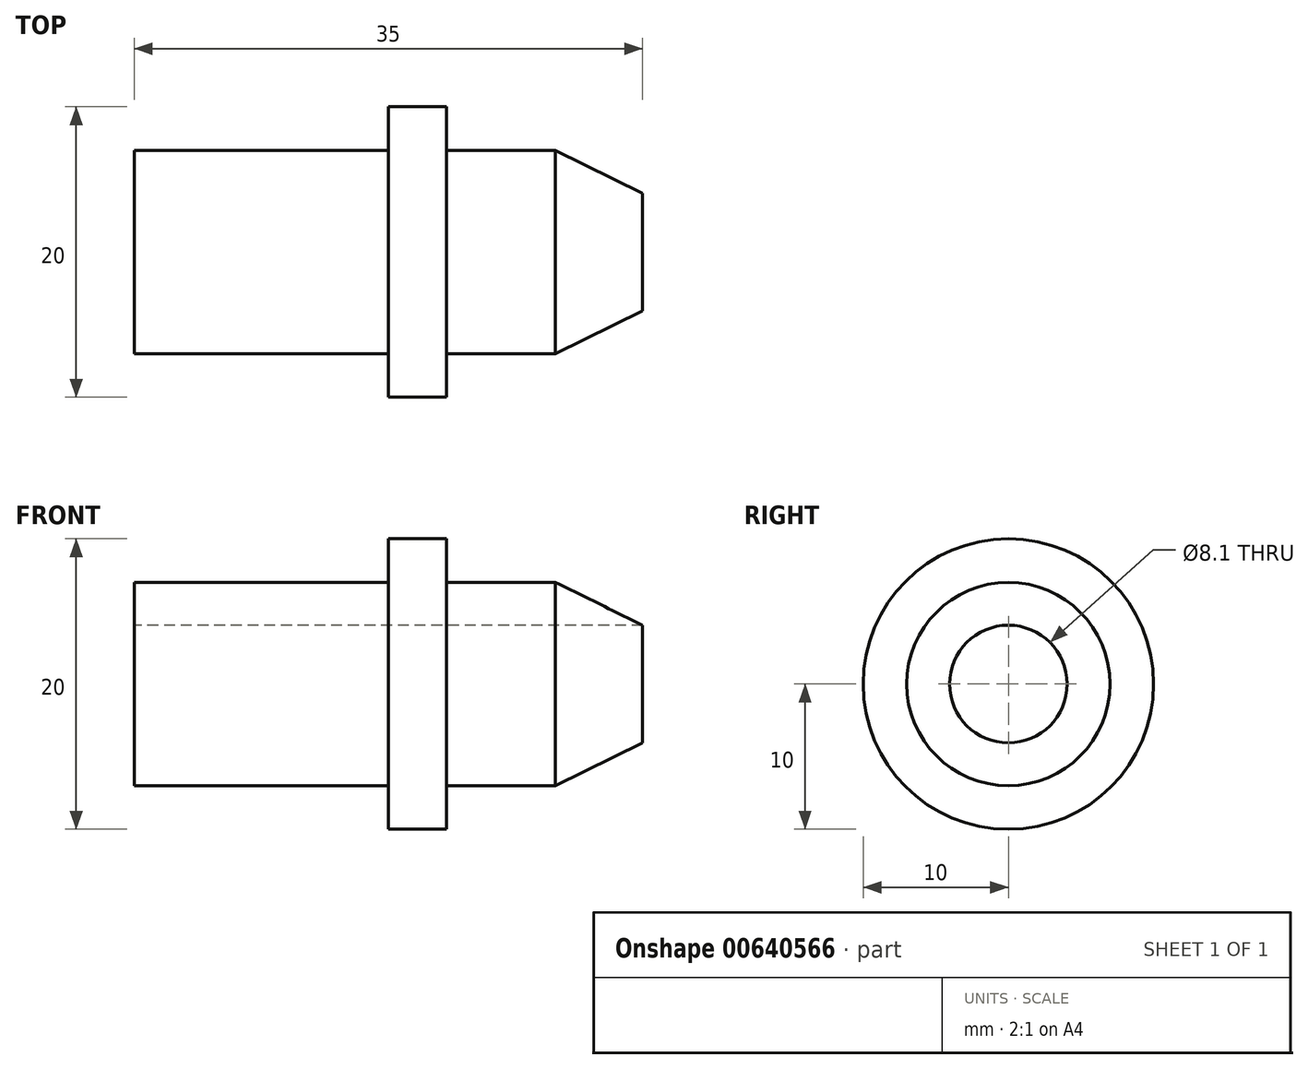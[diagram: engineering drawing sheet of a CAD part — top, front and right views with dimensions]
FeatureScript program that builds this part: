
annotation { "Feature Type Name" : "Feature", "Feature Type Description" : "" }
export const myFeature = defineFeature(function(context is Context, id is Id, definition is map)
    precondition{}
    {
        {
            var Q0;
            Q0=qCreatedBy(makeId("Front.planeOp"),FACE);
            var sketch = newSketch(context, id + "F0", { "sketchPlane" : qUnion([Q0])});
            skLineSegment(sketch, "E0", {"start": v(0, 4.05) * mm, "end": v(0, 7) * mm});
            skLineSegment(sketch, "E1", {"start": v(0, 7) * mm, "end": v(29, 7) * mm});
            skLineSegment(sketch, "E2", {"start": v(29, 7) * mm, "end": v(35, 4.05) * mm});
            skLineSegment(sketch, "E3", {"start": v(35, 4.05) * mm, "end": v(0, 4.05) * mm});
            skLineSegment(sketch, "E4", {"start": v(0, 0) * mm, "end": v(24.78, 0) * mm, "construction": true});
            skSolve(sketch);
        }
        {
            var Q0;
            Q0 = qSketchRegion(id + "F0", true);
            var Q1;
            Q1=sQuery(id+"F0.wireOp",EDGE,"E4");
            revolve(context, id + "F1", {"entities" : qUnion([Q0]), "axis" : qUnion([Q1]), "revolveType" : RevolveType.FULL});
        }
        {
            var Q0;
            Q0=qCreatedBy(makeId("Front.planeOp"),FACE);
            var sketch = newSketch(context, id + "F2", { "sketchPlane" : qUnion([Q0])});
            skLineSegment(sketch, "E5.bottom", {"start": v(17.5, 10) * mm, "end": v(21.5, 10) * mm});
            skLineSegment(sketch, "E5.top", {"start": v(17.5, 7) * mm, "end": v(21.5, 7) * mm});
            skLineSegment(sketch, "E5.left", {"start": v(17.5, 10) * mm, "end": v(17.5, 7) * mm});
            skLineSegment(sketch, "E5.right", {"start": v(21.5, 10) * mm, "end": v(21.5, 7) * mm});
            skSolve(sketch);
        }
        {
            var Q0;
            Q0 = qSketchRegion(id + "F2", true);
            var Q1;
            Q1=sQuery(id+"F0.wireOp",EDGE,"E4");
            revolve(context, id + "F3", {"operationType" : NewBodyOperationType.ADD, "entities" : qUnion([Q0]), "axis" : qUnion([Q1]), "revolveType" : RevolveType.FULL});
        }
    });
